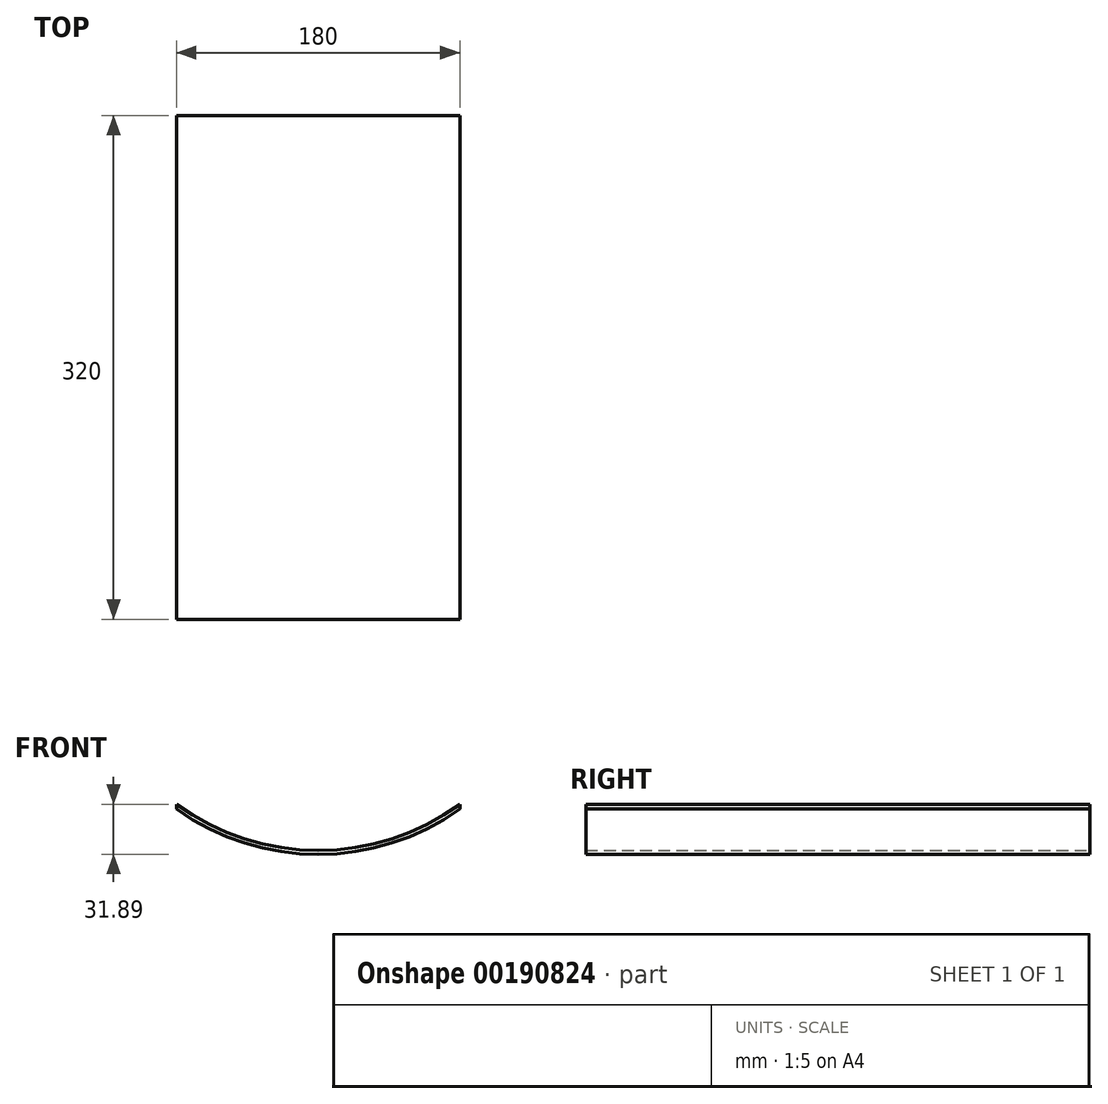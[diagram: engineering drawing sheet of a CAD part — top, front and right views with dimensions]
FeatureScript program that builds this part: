
annotation { "Feature Type Name" : "Feature", "Feature Type Description" : "" }
export const myFeature = defineFeature(function(context is Context, id is Id, definition is map)
    precondition{}
    {
        {
            var Q0;
            Q0=qCreatedBy(makeId("Front.planeOp"),FACE);
            var sketch = newSketch(context, id + "F0", { "sketchPlane" : qUnion([Q0])});
            skArc(sketch, "E0", {"start": v(-90, -123.11) * mm, "mid": v(0, -152.5) * mm, "end": v(90, -123.11) * mm});
            skArc(sketch, "E1", {"start": v(-90, -126.2) * mm, "mid": v(0, -155) * mm, "end": v(90, -126.2) * mm});
            skLineSegment(sketch, "E2", {"start": v(90, -123.11) * mm, "end": v(90, -126.2) * mm});
            skLineSegment(sketch, "E3", {"start": v(-90, -123.11) * mm, "end": v(-90, -126.2) * mm});
            skSolve(sketch);
        }
        {
            var Q0;
            Q0 = qSketchRegion(id + "F0", true);
            extrude(context, id + "F1", {"entities" : qUnion([Q0]), "depth" : 320 * mm});
        }
    });
